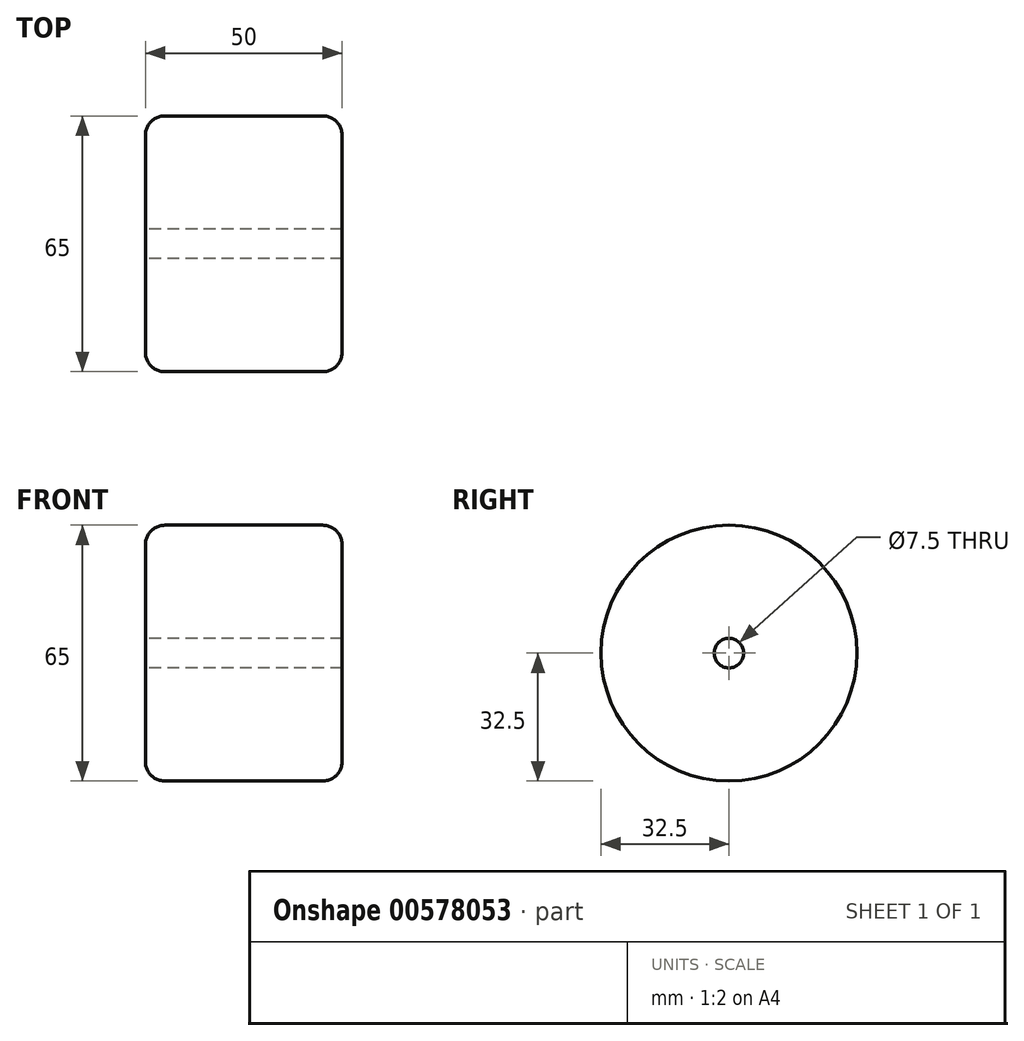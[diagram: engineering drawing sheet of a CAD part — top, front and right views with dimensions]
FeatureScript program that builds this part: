
annotation { "Feature Type Name" : "Feature", "Feature Type Description" : "" }
export const myFeature = defineFeature(function(context is Context, id is Id, definition is map)
    precondition{}
    {
        {
            var Q0;
            Q0=qCreatedBy(makeId("Right.planeOp"),FACE);
            var sketch = newSketch(context, id + "F0", { "sketchPlane" : qUnion([Q0])});
            skCircle(sketch, "E0", {"center": v(0, 0) * mm, "radius": 3.75 * mm});
            skCircle(sketch, "E1", {"center": v(0, 0) * mm, "radius": 32.5 * mm});
            skSolve(sketch);
        }
        {
            var Q0;
            Q0 = qSketchRegion(id + "F0", true);
            extrude(context, id + "F1", {"entities" : qUnion([Q0]), "depth" : 50 * mm, "offsetDistance" : 25 * mm});
        }
        {
            var Q0;
            Q0=makeQuery(id+"F1.opExtrude","CAP_EDGE",EDGE,{"disambiguationData":[OSD([sQuery(id+"F0.wireOp",EDGE,"E1")])],"isStart":false});
            var Q1;
            Q1=makeQuery(id+"F1.opExtrude","CAP_EDGE",EDGE,{"disambiguationData":[OSD([sQuery(id+"F0.wireOp",EDGE,"E1")])],"isStart":true});
            fillet(context, id + "F2", {"entities" : qUnion([Q0, Q1]), "radius" : 5 * mm, "tangentPropagation" : true, "allowEdgeOverflow" : false});
        }
    });
